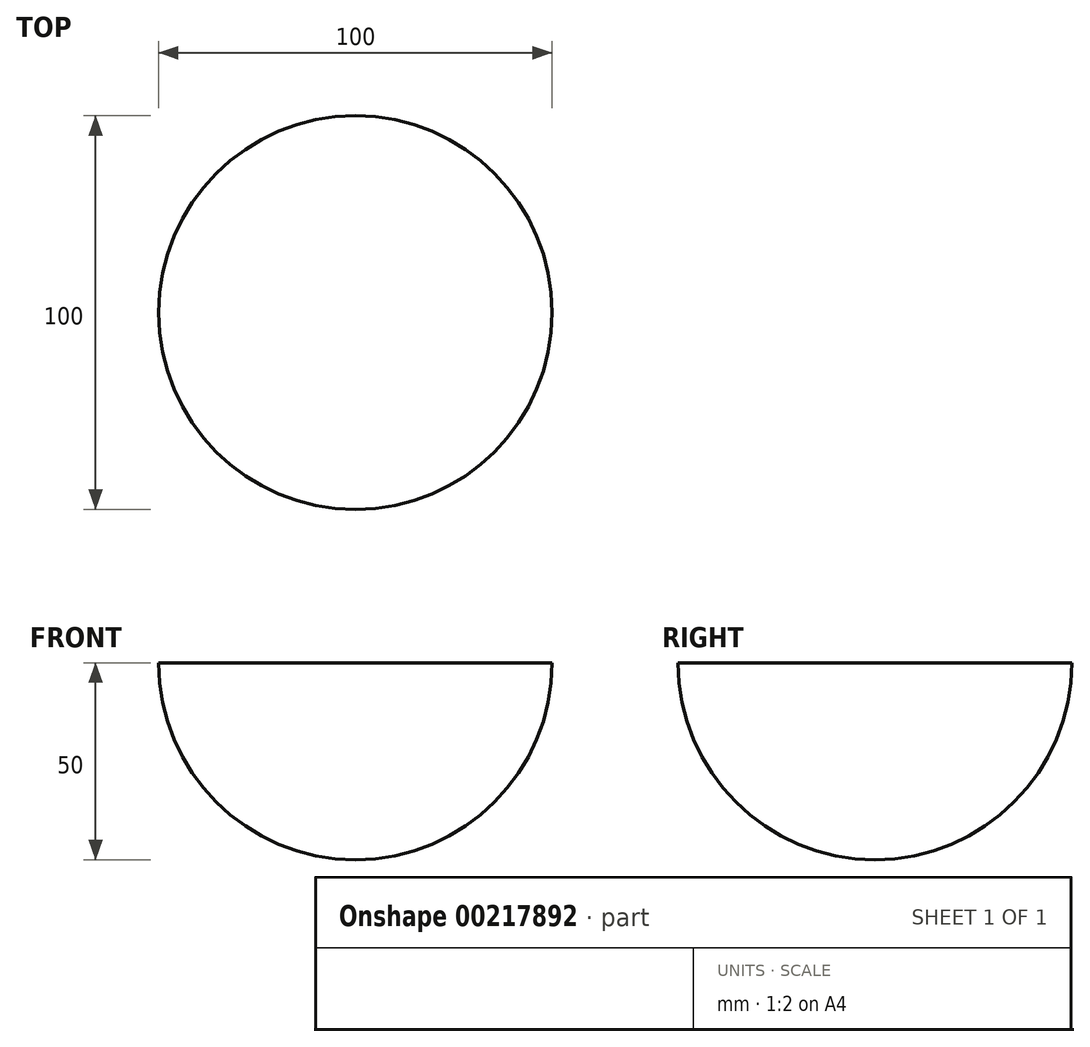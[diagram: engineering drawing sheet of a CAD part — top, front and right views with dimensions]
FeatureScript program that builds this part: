
annotation { "Feature Type Name" : "Feature", "Feature Type Description" : "" }
export const myFeature = defineFeature(function(context is Context, id is Id, definition is map)
    precondition{}
    {
        {
            var Q0;
            Q0=qCreatedBy(makeId("Top.planeOp"),FACE);
            var sketch = newSketch(context, id + "F0", { "sketchPlane" : qUnion([Q0])});
            skArc(sketch, "E0", {"start": v(50, 0) * mm, "mid": v(0, 50) * mm, "end": v(-50, 0) * mm});
            skLineSegment(sketch, "E1", {"start": v(-50, 0) * mm, "end": v(50, 0) * mm});
            skSolve(sketch);
        }
        {
            var Q0;
            Q0=sQuery(id+"F0.wireOp",EDGE,"E0");
            var Q1;
            Q1=sQuery(id+"F0.wireOp",EDGE,"E1");
            revolve(context, id + "F1", {"bodyType" : ToolBodyType.SURFACE, "surfaceEntities" : qUnion([Q0]), "axis" : qUnion([Q1]), "revolveType" : RevolveType.ONE_DIRECTION, "oppositeDirection" : true, "angle" : 180 * degree});
        }
    });
